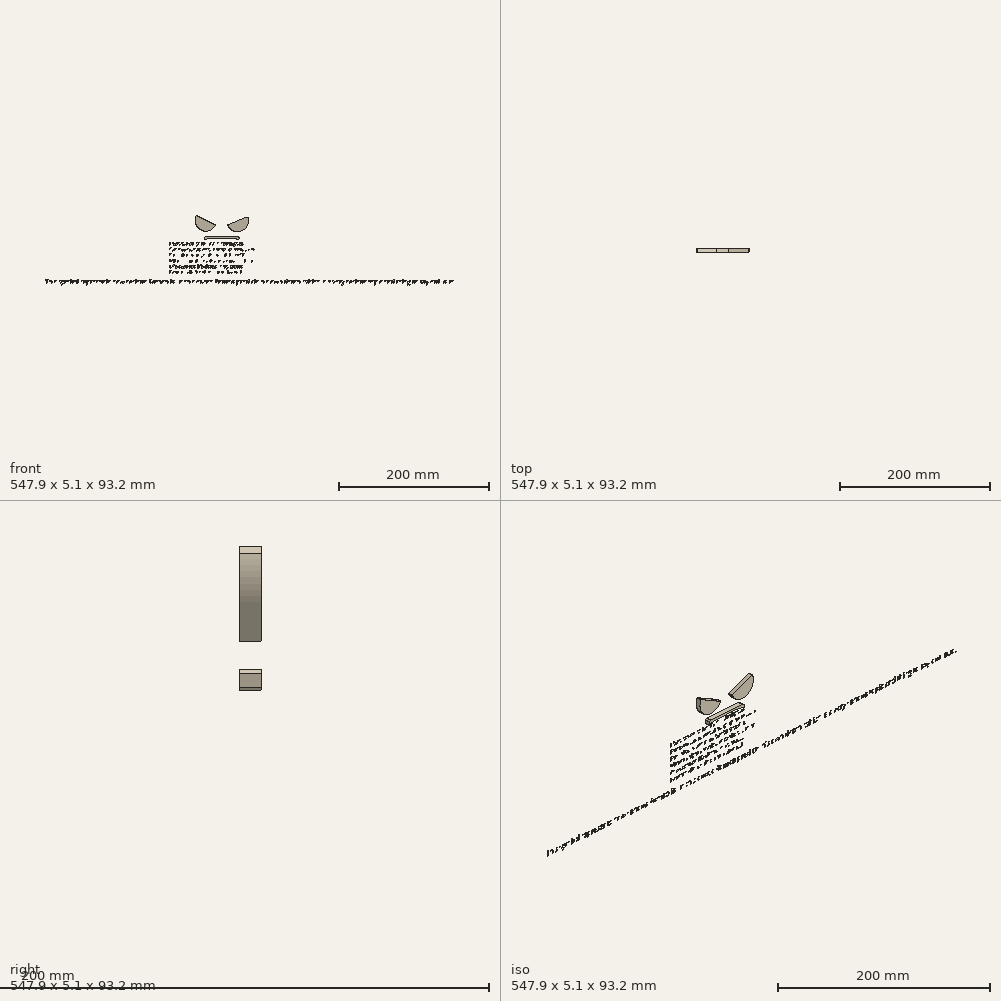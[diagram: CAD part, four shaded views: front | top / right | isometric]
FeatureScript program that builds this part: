
annotation { "Feature Type Name" : "Feature", "Feature Type Description" : "" }
export const myFeature = defineFeature(function(context is Context, id is Id, definition is map)
    precondition{}
    {
        {
            var Q0;
            Q0=qCreatedBy(makeId("Front.planeOp"),FACE);
            var sketch = newSketch(context, id + "F0", { "sketchPlane" : qUnion([Q0])});
            skCircle(sketch, "E0", {"center": v(-22.02, 21.65) * mm, "radius": 14.6 * mm});
            skCircle(sketch, "E1", {"center": v(20.22, 20.87) * mm, "radius": 14.6 * mm});
            skLineSegment(sketch, "E2", {"start": v(-35.17, 27.98) * mm, "end": v(-8.87, 15.32) * mm});
            skLineSegment(sketch, "E3", {"start": v(6.73, 15.32) * mm, "end": v(33.72, 26.43) * mm});
            skLineSegment(sketch, "E4.bottom", {"start": v(-24.15, 0) * mm, "end": v(22.3, 0) * mm});
            skLineSegment(sketch, "E4.top", {"start": v(-24.15, -5.72) * mm, "end": v(22.3, -5.72) * mm});
            skLineSegment(sketch, "E4.left", {"start": v(-24.15, 0) * mm, "end": v(-24.15, -5.72) * mm});
            skLineSegment(sketch, "E4.right", {"start": v(22.3, 0) * mm, "end": v(22.3, -5.72) * mm});
            skFitSpline(sketch, "E5", {"points": [v(-24.15, -4.67) * mm, v(-18.69, -2.92) * mm, v(-11.52, -2.54) * mm, v(-2.68, -2.54) * mm, v(5.84, -2.42) * mm, v(14.56, -2.61) * mm, v(22.3, -4.05) * mm], "startDerivative": vector(36.83, 14.48) * mm, "endDerivative": vector(45.23, -10.36) * mm});
            skFitSpline(sketch, "E6", {"points": [v(-24.15, -0.9) * mm, v(-21.79, 0) * mm], "startDerivative": vector(2.36, 0.9) * mm, "endDerivative": vector(2.36, 0.9) * mm});
            skFitSpline(sketch, "E7", {"points": [v(22.3, -0.99) * mm, v(20.3, 0) * mm], "startDerivative": vector(-2, 0.99) * mm, "endDerivative": vector(-2, 0.99) * mm});
            skSolve(sketch);
        }
        {
            var Q0;
            {var subQ0=sQuery(id+"F0.wireOp",EDGE,"E2");Q0=makeQuery(id+"F0.imprint","IMPRINT",FACE,{"disambiguationData":[TD([[makeQuery(id+"F0.imprint","IMPRINT",EDGE,{"derivedFrom":subQ0}),-1.0]])]});}
            var Q1;
            {var subQ0=sQuery(id+"F0.wireOp",EDGE,"E3");Q1=makeQuery(id+"F0.imprint","IMPRINT",FACE,{"disambiguationData":[TD([[makeQuery(id+"F0.imprint","IMPRINT",EDGE,{"derivedFrom":subQ0}),-1.0]])]});}
            extrude(context, id + "F1", {"entities" : qUnion([Q0, Q1]), "depth" : 5.08 * mm, "offsetDistance" : 25.4 * mm});
        }
        {
            var Q0;
            {var subQ0=sQuery(id+"F0.wireOp",EDGE,"E5");Q0=makeQuery(id+"F0.imprint","IMPRINT",FACE,{"disambiguationData":[TD([[makeQuery(id+"F0.imprint","IMPRINT",EDGE,{"derivedFrom":subQ0}),1.0]])]});}
            extrude(context, id + "F2", {"entities" : qUnion([Q0]), "depth" : 5.08 * mm, "offsetDistance" : 25.4 * mm});
        }
        {
            var Q0;
            Q0=qCreatedBy(makeId("Front.planeOp"),FACE);
            var sketch = newSketch(context, id + "F3", { "sketchPlane" : qUnion([Q0])});
            skText(sketch, "E8", { "text": "I fear, too early: for my mind misgives \nSome consequence yet hanging in the stars \nShall bitterly begin his fearful date 610\nWith this night\'s revels and expire the term \nOf a despised life closed in my breast \nBy some vile forfeit of untimely death", "fontName": "OpenSans-Regular.ttf"});
            const initialGuessF3  = {"E8": [-0.07098, -0.01161, 1, 0, 0.00406]};
            skSetInitialGuess(sketch, initialGuessF3);
            skSolve(sketch);
        }
        {
            var Q0;
            Q0=qCreatedBy(makeId("Front.planeOp"),FACE);
            var sketch = newSketch(context, id + "F4", { "sketchPlane" : qUnion([Q0])});
            skText(sketch, "E9", { "text": "This symbol represents how serious Romeo is. In this quote Romeo predicts his own death. which is a very serious topic and thing to say out loud. \n", "fontName": "OpenSans-Regular.ttf"});
            const initialGuessF4  = {"E9": [-0.2367, -0.06332, 1, 0, 0.00583]};
            skSetInitialGuess(sketch, initialGuessF4);
            skSolve(sketch);
        }
        {
            var Q0;
            Q0 = qSketchRegion(id + "F3", true);
            var Q1;
            Q1 = qSketchRegion(id + "F4", true);
            extrude(context, id + "F5", {"entities" : qUnion([Q0, Q1]), "depth" : 0.05 * mm, "offsetDistance" : 25.4 * mm});
        }
    });
